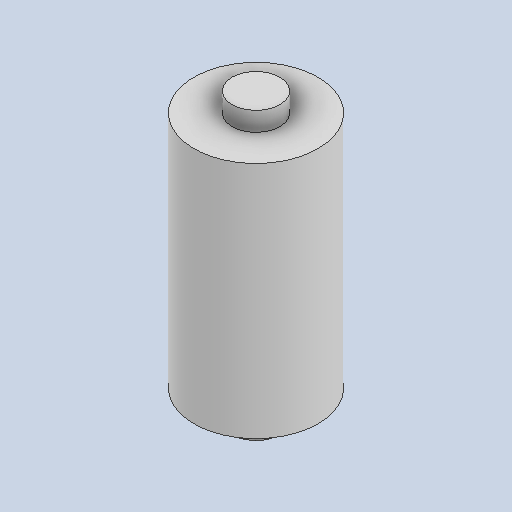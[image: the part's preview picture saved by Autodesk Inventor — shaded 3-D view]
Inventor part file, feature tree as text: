
AUTODESK INVENTOR PART (.ipt)
format: ipt  version: 2023 (Build 270158000, 158)  size: 229,888 bytes
history: native  units: in
note: dims shown in document units (in); Inventor stores cm internally (conversion verified against a paired STEP export)
features: extrude x2, sketch x2, plane x1
ambient origin geometry x8: Origin, YZ Plane, XZ Plane, XY Plane, X Axis, Y Axis, Z Axis, Center Point
bodies: Solid1 (feature_tree)
feature tree (5):
  extrude  "Extrusion1"  Depth=1.1811in TaperAngle=0.0deg
  plane  "Work Plane1"
  extrude  "Extrusion2"  Depth=0.9843in
  sketch  "Sketch1"  dims[d0=0.1969in d1=1.1811in d2=0.0in]
  sketch  "Sketch2"  dims[d3=-0.1181in d4=0.5118in d5=0.9843in d6=0.0in]
